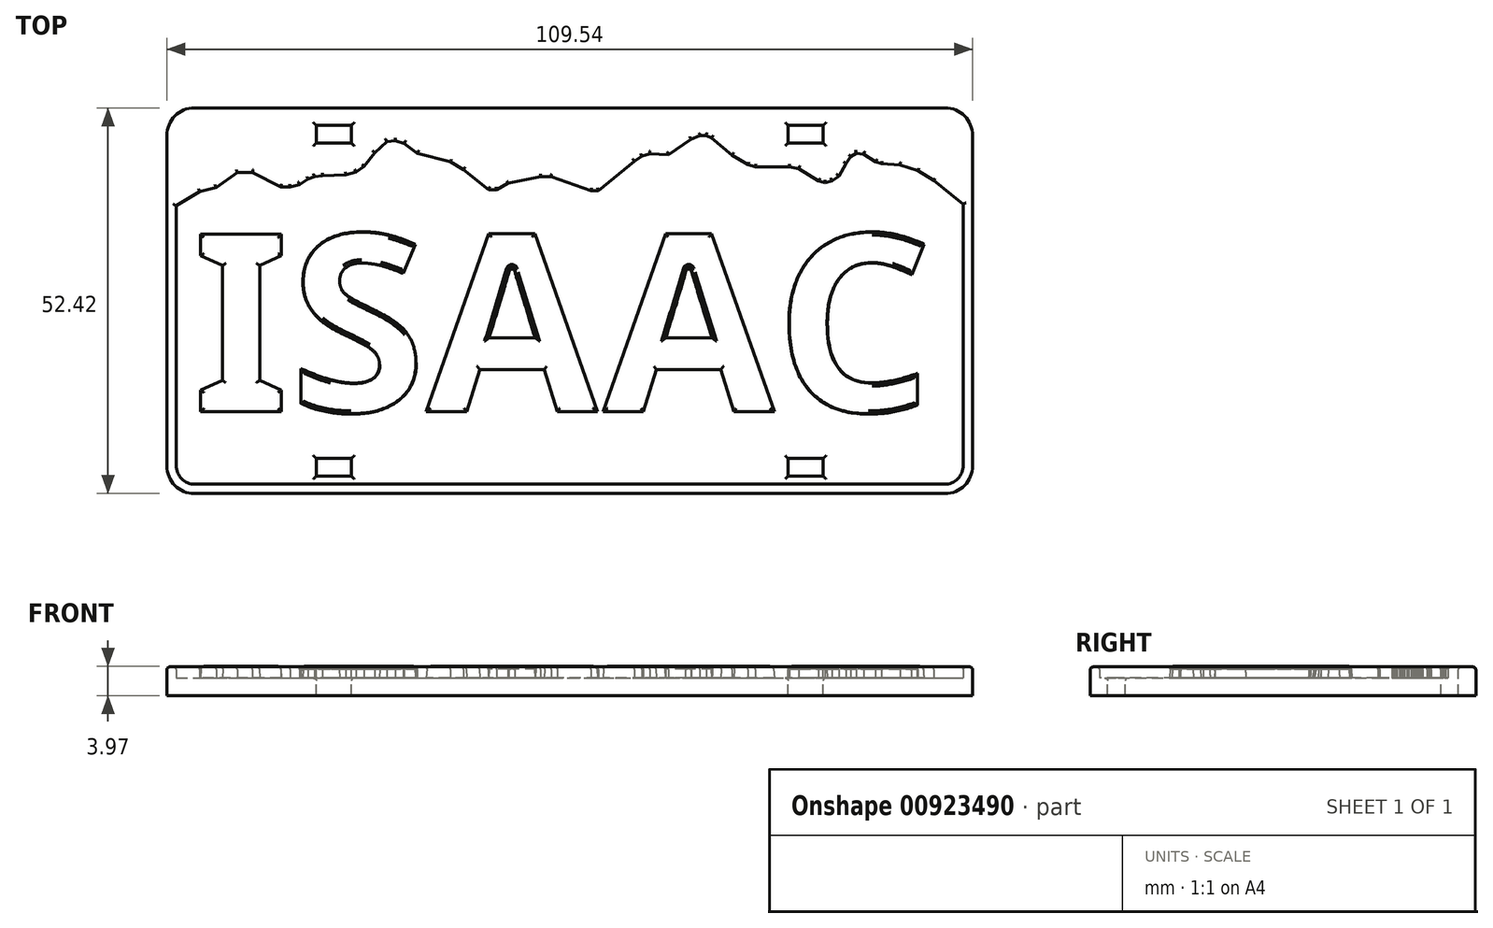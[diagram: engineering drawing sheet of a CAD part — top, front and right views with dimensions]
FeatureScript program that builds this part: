
annotation { "Feature Type Name" : "Feature", "Feature Type Description" : "" }
export const myFeature = defineFeature(function(context is Context, id is Id, definition is map)
    precondition{}
    {
        {
            var Q0;
            Q0=qCreatedBy(makeId("Top.planeOp"),FACE);
            var sketch = newSketch(context, id + "F0", { "sketchPlane" : qUnion([Q0])});
            skLineSegment(sketch, "E0", {"start": v(54.77, -22.46) * mm, "end": v(54.77, 22.46) * mm});
            skArc(sketch, "E1", {"start": v(54.77, 22.46) * mm, "mid": v(53.68, 25.11) * mm, "end": v(51.02, 26.21) * mm});
            skLineSegment(sketch, "E2", {"start": v(51.02, 26.21) * mm, "end": v(-51.02, 26.21) * mm});
            skArc(sketch, "E3", {"start": v(-51.02, 26.21) * mm, "mid": v(-53.68, 25.11) * mm, "end": v(-54.77, 22.46) * mm});
            skLineSegment(sketch, "E4", {"start": v(-54.77, 22.46) * mm, "end": v(-54.77, -22.46) * mm});
            skArc(sketch, "E5", {"start": v(-54.77, -22.46) * mm, "mid": v(-53.54, -25.24) * mm, "end": v(-50.64, -26.2) * mm});
            skLineSegment(sketch, "E6", {"start": v(-50.64, -26.2) * mm, "end": v(51.04, -26.2) * mm});
            skArc(sketch, "E7", {"start": v(51.02, -26.21) * mm, "mid": v(53.68, -25.11) * mm, "end": v(54.77, -22.46) * mm});
            skLineSegment(sketch, "E8", {"start": v(-54.77, 12.13) * mm, "end": v(-50.31, 14.84) * mm});
            skLineSegment(sketch, "E9", {"start": v(-50.31, 14.84) * mm, "end": v(-48.06, 15.4) * mm});
            skLineSegment(sketch, "E10", {"start": v(-48.06, 15.4) * mm, "end": v(-45.2, 17.44) * mm});
            skLineSegment(sketch, "E11", {"start": v(-45.2, 17.44) * mm, "end": v(-43.14, 17.44) * mm});
            skLineSegment(sketch, "E12", {"start": v(-43.14, 17.44) * mm, "end": v(-39.3, 15.5) * mm});
            skLineSegment(sketch, "E13", {"start": v(-39.3, 15.5) * mm, "end": v(-38.03, 15.49) * mm});
            skLineSegment(sketch, "E14", {"start": v(-38.03, 15.49) * mm, "end": v(-36.75, 15.8) * mm});
            skLineSegment(sketch, "E15", {"start": v(-36.75, 15.8) * mm, "end": v(-35.57, 16.54) * mm});
            skLineSegment(sketch, "E16", {"start": v(-35.57, 16.54) * mm, "end": v(-34.73, 16.88) * mm});
            skLineSegment(sketch, "E17", {"start": v(-34.73, 16.88) * mm, "end": v(-33.6, 17.01) * mm});
            skLineSegment(sketch, "E18", {"start": v(-33.6, 17.01) * mm, "end": v(-30.43, 17.11) * mm});
            skLineSegment(sketch, "E19", {"start": v(-29.05, 17.5) * mm, "end": v(-27.98, 18.27) * mm});
            skLineSegment(sketch, "E20", {"start": v(-27.98, 18.27) * mm, "end": v(-26.53, 20.14) * mm});
            skLineSegment(sketch, "E21", {"start": v(-26.53, 20.14) * mm, "end": v(-24.88, 21.63) * mm});
            skLineSegment(sketch, "E22", {"start": v(-24.88, 21.63) * mm, "end": v(-23.73, 21.77) * mm});
            skLineSegment(sketch, "E23", {"start": v(-22.5, 21.4) * mm, "end": v(-20.72, 20.04) * mm});
            skLineSegment(sketch, "E24", {"start": v(-16.23, 18.87) * mm, "end": v(-14.45, 17.85) * mm});
            skLineSegment(sketch, "E25", {"start": v(-14.45, 17.85) * mm, "end": v(-11.02, 15.1) * mm});
            skLineSegment(sketch, "E26", {"start": v(-11.02, 15.1) * mm, "end": v(-9.93, 15.1) * mm});
            skLineSegment(sketch, "E27", {"start": v(-9.93, 15.1) * mm, "end": v(-8.4, 15.96) * mm});
            skLineSegment(sketch, "E28", {"start": v(-8.4, 15.96) * mm, "end": v(-3.94, 16.85) * mm});
            skLineSegment(sketch, "E29", {"start": v(-3.94, 16.85) * mm, "end": v(-2.54, 16.85) * mm});
            skLineSegment(sketch, "E30", {"start": v(-2.54, 16.85) * mm, "end": v(2.9, 14.97) * mm});
            skLineSegment(sketch, "E31", {"start": v(2.9, 14.97) * mm, "end": v(3.92, 14.97) * mm});
            skLineSegment(sketch, "E32", {"start": v(3.92, 14.97) * mm, "end": v(8.8, 18.97) * mm});
            skLineSegment(sketch, "E33", {"start": v(8.8, 18.97) * mm, "end": v(9.82, 19.64) * mm});
            skLineSegment(sketch, "E34", {"start": v(9.82, 19.64) * mm, "end": v(10.9, 19.97) * mm});
            skLineSegment(sketch, "E35", {"start": v(10.9, 19.97) * mm, "end": v(13.43, 19.86) * mm});
            skLineSegment(sketch, "E36", {"start": v(16.5, 21.96) * mm, "end": v(17.71, 22.42) * mm});
            skLineSegment(sketch, "E37", {"start": v(17.71, 22.42) * mm, "end": v(18.56, 22.45) * mm});
            skLineSegment(sketch, "E38", {"start": v(18.56, 22.45) * mm, "end": v(19.28, 22.13) * mm});
            skLineSegment(sketch, "E39", {"start": v(19.28, 22.13) * mm, "end": v(22.05, 19.8) * mm});
            skLineSegment(sketch, "E40", {"start": v(22.05, 19.8) * mm, "end": v(24.2, 18.5) * mm});
            skLineSegment(sketch, "E41", {"start": v(24.2, 18.5) * mm, "end": v(25.23, 18.2) * mm});
            skLineSegment(sketch, "E42", {"start": v(25.23, 18.2) * mm, "end": v(29.85, 18.2) * mm});
            skLineSegment(sketch, "E43", {"start": v(29.85, 18.2) * mm, "end": v(31.13, 17.95) * mm});
            skLineSegment(sketch, "E44", {"start": v(31.13, 17.95) * mm, "end": v(33.84, 16.27) * mm});
            skLineSegment(sketch, "E45", {"start": v(33.84, 16.27) * mm, "end": v(34.73, 16.06) * mm});
            skLineSegment(sketch, "E46", {"start": v(34.73, 16.06) * mm, "end": v(35.67, 16.3) * mm});
            skLineSegment(sketch, "E47", {"start": v(35.67, 16.3) * mm, "end": v(36.58, 16.95) * mm});
            skLineSegment(sketch, "E48", {"start": v(36.58, 16.95) * mm, "end": v(37.58, 18.67) * mm});
            skLineSegment(sketch, "E49", {"start": v(38.22, 19.58) * mm, "end": v(38.96, 20.06) * mm});
            skLineSegment(sketch, "E50", {"start": v(38.96, 20.06) * mm, "end": v(39.94, 19.92) * mm});
            skLineSegment(sketch, "E51", {"start": v(41.58, 18.88) * mm, "end": v(42.4, 18.61) * mm});
            skLineSegment(sketch, "E52", {"start": v(42.4, 18.61) * mm, "end": v(44.9, 18.47) * mm});
            skLineSegment(sketch, "E53", {"start": v(44.9, 18.47) * mm, "end": v(47.31, 17.68) * mm});
            skLineSegment(sketch, "E54", {"start": v(47.31, 17.68) * mm, "end": v(49.47, 16.33) * mm});
            skLineSegment(sketch, "E55", {"start": v(49.47, 16.33) * mm, "end": v(51.88, 14.42) * mm});
            skLineSegment(sketch, "E56", {"start": v(51.88, 14.42) * mm, "end": v(53.78, 12.92) * mm});
            skLineSegment(sketch, "E57", {"start": v(53.78, 12.92) * mm, "end": v(54.77, 12.06) * mm});
            skLineSegment(sketch, "E58", {"start": v(-20.72, 20.04) * mm, "end": v(-16.23, 18.87) * mm});
            skLineSegment(sketch, "E59", {"start": v(16.5, 21.96) * mm, "end": v(13.43, 19.86) * mm});
            skLineSegment(sketch, "E60", {"start": v(-22.5, 21.4) * mm, "end": v(-23.73, 21.77) * mm});
            skLineSegment(sketch, "E61", {"start": v(-29.05, 17.5) * mm, "end": v(-30.43, 17.11) * mm});
            skLineSegment(sketch, "E62", {"start": v(37.58, 18.67) * mm, "end": v(38.22, 19.58) * mm});
            skLineSegment(sketch, "E63", {"start": v(41.58, 18.88) * mm, "end": v(39.94, 19.92) * mm});
            skSolve(sketch);
        }
        {
            var Q0;
            Q0=qCreatedBy(makeId("Top.planeOp"),FACE);
            var sketch = newSketch(context, id + "F1", { "sketchPlane" : qUnion([Q0])});
            skLineSegment(sketch, "E64", {"start": v(54.77, -22.46) * mm, "end": v(54.77, 22.46) * mm});
            skArc(sketch, "E65", {"start": v(54.77, 22.46) * mm, "mid": v(53.68, 25.11) * mm, "end": v(51.02, 26.21) * mm});
            skLineSegment(sketch, "E66", {"start": v(51.02, 26.21) * mm, "end": v(-51.02, 26.21) * mm});
            skArc(sketch, "E67", {"start": v(-51.02, 26.21) * mm, "mid": v(-53.68, 25.11) * mm, "end": v(-54.77, 22.46) * mm});
            skLineSegment(sketch, "E68", {"start": v(-54.77, 22.46) * mm, "end": v(-54.77, -22.46) * mm});
            skArc(sketch, "E69", {"start": v(-54.77, -22.46) * mm, "mid": v(-53.68, -25.11) * mm, "end": v(-51.02, -26.21) * mm});
            skLineSegment(sketch, "E70", {"start": v(-51.02, -26.21) * mm, "end": v(51.02, -26.21) * mm});
            skArc(sketch, "E71", {"start": v(51.02, -26.21) * mm, "mid": v(53.68, -25.11) * mm, "end": v(54.77, -22.46) * mm});
            skLineSegment(sketch, "E72.0", {"start": v(50.96, 24.94) * mm, "end": v(-50.96, 24.94) * mm, "construction": true});
            skLineSegment(sketch, "E72.1", {"start": v(53.5, -22.4) * mm, "end": v(53.5, 22.4) * mm, "construction": true});
            skLineSegment(sketch, "E72.2", {"start": v(-50.96, -24.94) * mm, "end": v(50.96, -24.94) * mm, "construction": true});
            skLineSegment(sketch, "E72.3", {"start": v(-53.5, 22.4) * mm, "end": v(-53.5, -22.4) * mm, "construction": true});
            skPoint(sketch, "E73.visualSharp", {"position": v(-53.5, 24.94) * mm});
            skArc(sketch, "E73.filletArc", {"start": v(-50.96, 24.94) * mm, "mid": v(-52.76, 24.2) * mm, "end": v(-53.5, 22.4) * mm, "construction": true});
            skPoint(sketch, "E74.visualSharp", {"position": v(-53.5, -24.94) * mm});
            skArc(sketch, "E74.filletArc", {"start": v(-53.5, -22.4) * mm, "mid": v(-52.76, -24.2) * mm, "end": v(-50.96, -24.94) * mm, "construction": true});
            skPoint(sketch, "E75.visualSharp", {"position": v(53.5, -24.94) * mm});
            skArc(sketch, "E75.filletArc", {"start": v(50.96, -24.94) * mm, "mid": v(52.76, -24.2) * mm, "end": v(53.5, -22.4) * mm, "construction": true});
            skPoint(sketch, "E76.visualSharp", {"position": v(53.5, 24.94) * mm});
            skArc(sketch, "E76.filletArc", {"start": v(53.5, 22.4) * mm, "mid": v(52.76, 24.2) * mm, "end": v(50.96, 24.94) * mm, "construction": true});
            skSolve(sketch);
        }
        {
            var Q0;
            {var subQ3=sQuery(id+"F0.wireOp",EDGE,"E1");Q0=makeQuery(id+"F0.imprint","IMPRINT",FACE,{"disambiguationData":[TD([[makeQuery(id+"F0.imprint","IMPRINT",EDGE,{"derivedFrom":subQ3}),1.0]])]});}
            extrude(context, id + "F2", {"entities" : qUnion([Q0]), "depth" : 1.52 * mm, "offsetDistance" : 25.4 * mm});
        }
        {
            var Q0;
            Q0=qSketchRegion(id+"F1",true);
            extrude(context, id + "F3", {"entities" : qUnion([Q0]), "operationType" : NewBodyOperationType.ADD, "oppositeDirection" : true, "depth" : 2.38 * mm, "offsetDistance" : 25.4 * mm});
        }
        {
            var Q0;
            {var subQ58=sQuery(id+"F0.wireOp",EDGE,"E0");var subQ59=sQuery(id+"F1.wireOp",EDGE,"E64");var subQ60=sQuery(id+"F1.wireOp",EDGE,"E65");var subQ61=sQuery(id+"F1.wireOp",EDGE,"E68");var subQ62=sQuery(id+"F1.wireOp",EDGE,"E69");var subQ63=sQuery(id+"F1.wireOp",EDGE,"E70");var subQ64=sQuery(id+"F1.wireOp",EDGE,"E71");Q0=makeQuery(id+"F3.boolean.opBoolean","SPLIT",FACE,{"disambiguationData":[TD([makeQuery(id+"F2.opExtrude","SWEPT_FACE",FACE,{"disambiguationData":[OSD([subQ58])]})])],"derivedFrom":makeQuery(id+"F3.opExtrude","CAP_FACE",FACE,{"disambiguationData":[OSD([subQ59,subQ60,sQuery(id+"F1.wireOp",EDGE,"E66"),sQuery(id+"F1.wireOp",EDGE,"E67"),subQ61,subQ62,subQ63,subQ64])],"isStart":true})});}
            var sketch = newSketch(context, id + "F4", { "sketchPlane" : qUnion([Q0])});
            skLineSegment(sketch, "E77", {"start": v(54.77, -22.46) * mm, "end": v(54.77, 12.06) * mm});
            skLineSegment(sketch, "E78", {"start": v(-54.77, 12.13) * mm, "end": v(-54.77, -22.46) * mm});
            skArc(sketch, "E79", {"start": v(-54.77, -22.46) * mm, "mid": v(-53.68, -25.11) * mm, "end": v(-51.02, -26.21) * mm});
            skLineSegment(sketch, "E80", {"start": v(-51.02, -26.21) * mm, "end": v(51.02, -26.21) * mm});
            skArc(sketch, "E81", {"start": v(51.02, -26.21) * mm, "mid": v(53.68, -25.11) * mm, "end": v(54.77, -22.46) * mm});
            skLineSegment(sketch, "E82.1", {"start": v(53.5, -22.4) * mm, "end": v(53.5, 13.14) * mm});
            skLineSegment(sketch, "E82.2", {"start": v(-50.96, -24.94) * mm, "end": v(50.96, -24.94) * mm});
            skLineSegment(sketch, "E82.3", {"start": v(-53.5, 12.9) * mm, "end": v(-53.5, -22.4) * mm});
            skPoint(sketch, "E83.visualSharp", {"position": v(-53.5, 24.94) * mm});
            skPoint(sketch, "E84.visualSharp", {"position": v(-53.5, -24.94) * mm});
            skArc(sketch, "E84.filletArc", {"start": v(-53.5, -22.4) * mm, "mid": v(-52.76, -24.2) * mm, "end": v(-50.96, -24.94) * mm});
            skPoint(sketch, "E85.visualSharp", {"position": v(53.5, -24.94) * mm});
            skArc(sketch, "E85.filletArc", {"start": v(50.96, -24.94) * mm, "mid": v(52.76, -24.2) * mm, "end": v(53.5, -22.4) * mm});
            skPoint(sketch, "E86.visualSharp", {"position": v(53.5, 24.94) * mm});
            skLineSegment(sketch, "E87", {"start": v(-54.77, 12.13) * mm, "end": v(-53.5, 12.9) * mm});
            skLineSegment(sketch, "E88", {"start": v(53.5, 13.14) * mm, "end": v(53.78, 12.92) * mm});
            skLineSegment(sketch, "E89", {"start": v(53.78, 12.92) * mm, "end": v(54.77, 12.06) * mm});
            skSolve(sketch);
        }
        {
            var Q0;
            Q0=qSketchRegion(id+"F4",true);
            extrude(context, id + "F5", {"entities" : qUnion([Q0]), "operationType" : NewBodyOperationType.ADD, "depth" : 1.52 * mm, "offsetDistance" : 25.4 * mm});
        }
        {
            var Q0;
            Q0=makeQuery(id+"F5.boolean.opBoolean","MERGE",FACE,{"derivedFrom":[makeQuery(id+"F2.opExtrude","CAP_FACE",FACE,{"disambiguationData":[OSD([sQuery(id+"F0.wireOp",EDGE,"E0"),sQuery(id+"F0.wireOp",EDGE,"E1"),sQuery(id+"F0.wireOp",EDGE,"E2"),sQuery(id+"F0.wireOp",EDGE,"E3"),sQuery(id+"F0.wireOp",EDGE,"E4"),sQuery(id+"F0.wireOp",EDGE,"E8"),sQuery(id+"F0.wireOp",EDGE,"E9"),sQuery(id+"F0.wireOp",EDGE,"E10"),sQuery(id+"F0.wireOp",EDGE,"E11"),sQuery(id+"F0.wireOp",EDGE,"E12"),sQuery(id+"F0.wireOp",EDGE,"E13"),sQuery(id+"F0.wireOp",EDGE,"E14"),sQuery(id+"F0.wireOp",EDGE,"E15"),sQuery(id+"F0.wireOp",EDGE,"E16"),sQuery(id+"F0.wireOp",EDGE,"E17"),sQuery(id+"F0.wireOp",EDGE,"E18"),sQuery(id+"F0.wireOp",EDGE,"7b9f405e-0691-426e-9c9e-a5372cf0836a"),sQuery(id+"F0.wireOp",EDGE,"E19"),sQuery(id+"F0.wireOp",EDGE,"E20"),sQuery(id+"F0.wireOp",EDGE,"E21"),sQuery(id+"F0.wireOp",EDGE,"E22"),sQuery(id+"F0.wireOp",EDGE,"b3dec5b1-662c-4d50-a13c-af7b7760114a"),sQuery(id+"F0.wireOp",EDGE,"E23"),sQuery(id+"F0.wireOp",EDGE,"4d9ee76e-0833-4cdc-b1a8-2d4ce76e6521"),sQuery(id+"F0.wireOp",EDGE,"E24"),sQuery(id+"F0.wireOp",EDGE,"E25"),sQuery(id+"F0.wireOp",EDGE,"E26"),sQuery(id+"F0.wireOp",EDGE,"E27"),sQuery(id+"F0.wireOp",EDGE,"E28"),sQuery(id+"F0.wireOp",EDGE,"E29"),sQuery(id+"F0.wireOp",EDGE,"E30"),sQuery(id+"F0.wireOp",EDGE,"E31"),sQuery(id+"F0.wireOp",EDGE,"E32"),sQuery(id+"F0.wireOp",EDGE,"E33"),sQuery(id+"F0.wireOp",EDGE,"E34"),sQuery(id+"F0.wireOp",EDGE,"E35"),sQuery(id+"F0.wireOp",EDGE,"55551997-bb9e-4b94-90c5-def3cb147476"),sQuery(id+"F0.wireOp",EDGE,"E36"),sQuery(id+"F0.wireOp",EDGE,"E37"),sQuery(id+"F0.wireOp",EDGE,"E38"),sQuery(id+"F0.wireOp",EDGE,"E39"),sQuery(id+"F0.wireOp",EDGE,"E40"),sQuery(id+"F0.wireOp",EDGE,"E41"),sQuery(id+"F0.wireOp",EDGE,"E42"),sQuery(id+"F0.wireOp",EDGE,"E43"),sQuery(id+"F0.wireOp",EDGE,"E44"),sQuery(id+"F0.wireOp",EDGE,"E45"),sQuery(id+"F0.wireOp",EDGE,"E46"),sQuery(id+"F0.wireOp",EDGE,"E47"),sQuery(id+"F0.wireOp",EDGE,"E48"),sQuery(id+"F0.wireOp",EDGE,"513b7cbe-d979-4e22-b277-f3c42ccdbda1"),sQuery(id+"F0.wireOp",EDGE,"E49"),sQuery(id+"F0.wireOp",EDGE,"E50"),sQuery(id+"F0.wireOp",EDGE,"0d842e13-672c-40e3-aae4-28923e78d4e0"),sQuery(id+"F0.wireOp",EDGE,"E51"),sQuery(id+"F0.wireOp",EDGE,"E52"),sQuery(id+"F0.wireOp",EDGE,"E53"),sQuery(id+"F0.wireOp",EDGE,"E54"),sQuery(id+"F0.wireOp",EDGE,"E55"),sQuery(id+"F0.wireOp",EDGE,"E56"),sQuery(id+"F0.wireOp",EDGE,"E57")])],"isStart":false}),makeQuery(id+"F5.opExtrude","CAP_FACE",FACE,{"disambiguationData":[OSD([sQuery(id+"F4.wireOp",EDGE,"E77"),sQuery(id+"F4.wireOp",EDGE,"E78"),sQuery(id+"F4.wireOp",EDGE,"E79"),sQuery(id+"F4.wireOp",EDGE,"E80"),sQuery(id+"F4.wireOp",EDGE,"E81"),sQuery(id+"F4.wireOp",EDGE,"E82.1"),sQuery(id+"F4.wireOp",EDGE,"E82.2"),sQuery(id+"F4.wireOp",EDGE,"E82.3"),sQuery(id+"F4.wireOp",EDGE,"E84.filletArc"),sQuery(id+"F4.wireOp",EDGE,"E85.filletArc"),sQuery(id+"F4.wireOp",EDGE,"E87"),sQuery(id+"F4.wireOp",EDGE,"E88"),sQuery(id+"F4.wireOp",EDGE,"E89")])],"isStart":false})]});
            var sketch = newSketch(context, id + "F6", { "sketchPlane" : qUnion([Q0])});
            skLineSegment(sketch, "E90.bottom", {"start": v(-34.45, 23.83) * mm, "end": v(-29.7, 23.83) * mm});
            skLineSegment(sketch, "E90.top", {"start": v(-34.45, 21.45) * mm, "end": v(-29.7, 21.45) * mm});
            skLineSegment(sketch, "E90.left", {"start": v(-34.45, 23.83) * mm, "end": v(-34.45, 21.45) * mm});
            skLineSegment(sketch, "E90.right", {"start": v(-29.7, 23.83) * mm, "end": v(-29.7, 21.45) * mm});
            skLineSegment(sketch, "E91", {"start": v(0, 26.21) * mm, "end": v(0, -26.21) * mm, "construction": true});
            skLineSegment(sketch, "E92.MirrorCS", {"start": v(34.45, 23.83) * mm, "end": v(34.45, 21.45) * mm});
            skLineSegment(sketch, "E93.MirrorCS", {"start": v(29.7, 23.83) * mm, "end": v(29.7, 21.45) * mm});
            skLineSegment(sketch, "E94.MirrorCS", {"start": v(34.45, 21.45) * mm, "end": v(29.7, 21.45) * mm});
            skLineSegment(sketch, "E95.MirrorCS", {"start": v(34.45, 23.83) * mm, "end": v(29.7, 23.83) * mm});
            skLineSegment(sketch, "E96", {"start": v(0, 0) * mm, "end": v(-59.23, 0) * mm, "construction": true});
            skLineSegment(sketch, "E97", {"start": v(0, 0) * mm, "end": v(56.47, 0) * mm, "construction": true});
            skLineSegment(sketch, "E98.MirrorCS", {"start": v(-34.45, -23.83) * mm, "end": v(-29.7, -23.83) * mm});
            skLineSegment(sketch, "E99.MirrorCS", {"start": v(-34.45, -23.83) * mm, "end": v(-34.45, -21.45) * mm});
            skLineSegment(sketch, "E100.MirrorCS", {"start": v(-34.45, -21.45) * mm, "end": v(-29.7, -21.45) * mm});
            skLineSegment(sketch, "E101.MirrorCS", {"start": v(-29.7, -23.83) * mm, "end": v(-29.7, -21.45) * mm});
            skLineSegment(sketch, "E102.MirrorCS", {"start": v(29.7, -23.83) * mm, "end": v(29.7, -21.45) * mm});
            skLineSegment(sketch, "E103.MirrorCS", {"start": v(34.45, -23.83) * mm, "end": v(29.7, -23.83) * mm});
            skLineSegment(sketch, "E104.MirrorCS", {"start": v(34.45, -23.83) * mm, "end": v(34.45, -21.45) * mm});
            skLineSegment(sketch, "E105.MirrorCS", {"start": v(34.45, -21.45) * mm, "end": v(29.7, -21.45) * mm});
            skSolve(sketch);
        }
        {
            var Q0;
            Q0=qSketchRegion(id+"F6",true);
            extrude(context, id + "F7", {"entities" : qUnion([Q0]), "operationType" : NewBodyOperationType.REMOVE, "endBound" : BoundingType.THROUGH_ALL, "oppositeDirection" : true, "depth" : 25.4 * mm, "offsetDistance" : 25.4 * mm});
        }
        {
            var Q0;
            Q0=makeQuery(id+"F3.opExtrude","CAP_FACE",FACE,{"disambiguationData":[OSD([sQuery(id+"F1.wireOp",EDGE,"E64"),sQuery(id+"F1.wireOp",EDGE,"E65"),sQuery(id+"F1.wireOp",EDGE,"E66"),sQuery(id+"F1.wireOp",EDGE,"E67"),sQuery(id+"F1.wireOp",EDGE,"E68"),sQuery(id+"F1.wireOp",EDGE,"E69"),sQuery(id+"F1.wireOp",EDGE,"E70"),sQuery(id+"F1.wireOp",EDGE,"E71")])],"isStart":true});
            var sketch = newSketch(context, id + "F8", { "sketchPlane" : qUnion([Q0])});
            skText(sketch, "E106", { "text": "ISAAC", "fontName": "NotoSans-Bold.ttf"});
            const initialGuessF8  = {"E106": [-0.05126, -0.01508, 1, 0, 0.02432]};
            skSetInitialGuess(sketch, initialGuessF8);
            skSolve(sketch);
        }
        {
            var Q0;
            Q0=qSketchRegion(id+"F8",true);
            extrude(context, id + "F9", {"entities" : qUnion([Q0]), "operationType" : NewBodyOperationType.ADD, "depth" : 1.59 * mm, "offsetDistance" : 25.4 * mm, "hasDraft" : true, "draftAngle" : 3 * degree, "draftPullDirection" : true});
        }
        {
            var Q0;
            Q0=makeQuery(id+"F5.boolean.opBoolean","MERGE",FACE,{"derivedFrom":[makeQuery(id+"F2.opExtrude","CAP_FACE",FACE,{"disambiguationData":[OSD([sQuery(id+"F0.wireOp",EDGE,"E0"),sQuery(id+"F0.wireOp",EDGE,"E1"),sQuery(id+"F0.wireOp",EDGE,"E2"),sQuery(id+"F0.wireOp",EDGE,"E3"),sQuery(id+"F0.wireOp",EDGE,"E4"),sQuery(id+"F0.wireOp",EDGE,"E8"),sQuery(id+"F0.wireOp",EDGE,"E9"),sQuery(id+"F0.wireOp",EDGE,"E10"),sQuery(id+"F0.wireOp",EDGE,"E11"),sQuery(id+"F0.wireOp",EDGE,"E12"),sQuery(id+"F0.wireOp",EDGE,"E13"),sQuery(id+"F0.wireOp",EDGE,"E14"),sQuery(id+"F0.wireOp",EDGE,"E15"),sQuery(id+"F0.wireOp",EDGE,"E16"),sQuery(id+"F0.wireOp",EDGE,"E17"),sQuery(id+"F0.wireOp",EDGE,"E18"),sQuery(id+"F0.wireOp",EDGE,"7b9f405e-0691-426e-9c9e-a5372cf0836a"),sQuery(id+"F0.wireOp",EDGE,"E19"),sQuery(id+"F0.wireOp",EDGE,"E20"),sQuery(id+"F0.wireOp",EDGE,"E21"),sQuery(id+"F0.wireOp",EDGE,"E22"),sQuery(id+"F0.wireOp",EDGE,"b3dec5b1-662c-4d50-a13c-af7b7760114a"),sQuery(id+"F0.wireOp",EDGE,"E23"),sQuery(id+"F0.wireOp",EDGE,"4d9ee76e-0833-4cdc-b1a8-2d4ce76e6521"),sQuery(id+"F0.wireOp",EDGE,"E24"),sQuery(id+"F0.wireOp",EDGE,"E25"),sQuery(id+"F0.wireOp",EDGE,"E26"),sQuery(id+"F0.wireOp",EDGE,"E27"),sQuery(id+"F0.wireOp",EDGE,"E28"),sQuery(id+"F0.wireOp",EDGE,"E29"),sQuery(id+"F0.wireOp",EDGE,"E30"),sQuery(id+"F0.wireOp",EDGE,"E31"),sQuery(id+"F0.wireOp",EDGE,"E32"),sQuery(id+"F0.wireOp",EDGE,"E33"),sQuery(id+"F0.wireOp",EDGE,"E34"),sQuery(id+"F0.wireOp",EDGE,"E35"),sQuery(id+"F0.wireOp",EDGE,"55551997-bb9e-4b94-90c5-def3cb147476"),sQuery(id+"F0.wireOp",EDGE,"E36"),sQuery(id+"F0.wireOp",EDGE,"E37"),sQuery(id+"F0.wireOp",EDGE,"E38"),sQuery(id+"F0.wireOp",EDGE,"E39"),sQuery(id+"F0.wireOp",EDGE,"E40"),sQuery(id+"F0.wireOp",EDGE,"E41"),sQuery(id+"F0.wireOp",EDGE,"E42"),sQuery(id+"F0.wireOp",EDGE,"E43"),sQuery(id+"F0.wireOp",EDGE,"E44"),sQuery(id+"F0.wireOp",EDGE,"E45"),sQuery(id+"F0.wireOp",EDGE,"E46"),sQuery(id+"F0.wireOp",EDGE,"E47"),sQuery(id+"F0.wireOp",EDGE,"E48"),sQuery(id+"F0.wireOp",EDGE,"513b7cbe-d979-4e22-b277-f3c42ccdbda1"),sQuery(id+"F0.wireOp",EDGE,"E49"),sQuery(id+"F0.wireOp",EDGE,"E50"),sQuery(id+"F0.wireOp",EDGE,"0d842e13-672c-40e3-aae4-28923e78d4e0"),sQuery(id+"F0.wireOp",EDGE,"E51"),sQuery(id+"F0.wireOp",EDGE,"E52"),sQuery(id+"F0.wireOp",EDGE,"E53"),sQuery(id+"F0.wireOp",EDGE,"E54"),sQuery(id+"F0.wireOp",EDGE,"E55"),sQuery(id+"F0.wireOp",EDGE,"E56"),sQuery(id+"F0.wireOp",EDGE,"E57")])],"isStart":false}),makeQuery(id+"F5.opExtrude","CAP_FACE",FACE,{"disambiguationData":[OSD([sQuery(id+"F4.wireOp",EDGE,"E77"),sQuery(id+"F4.wireOp",EDGE,"E78"),sQuery(id+"F4.wireOp",EDGE,"E79"),sQuery(id+"F4.wireOp",EDGE,"E80"),sQuery(id+"F4.wireOp",EDGE,"E81"),sQuery(id+"F4.wireOp",EDGE,"E82.1"),sQuery(id+"F4.wireOp",EDGE,"E82.2"),sQuery(id+"F4.wireOp",EDGE,"E82.3"),sQuery(id+"F4.wireOp",EDGE,"E84.filletArc"),sQuery(id+"F4.wireOp",EDGE,"E85.filletArc"),sQuery(id+"F4.wireOp",EDGE,"E87"),sQuery(id+"F4.wireOp",EDGE,"E88"),sQuery(id+"F4.wireOp",EDGE,"E89")])],"isStart":false})]});
            var Q1;
            {var subQ0=sQuery(id+"F1.wireOp",EDGE,"E64");var subQ1=sQuery(id+"F1.wireOp",EDGE,"E68");var subQ2=sQuery(id+"F1.wireOp",EDGE,"E69");var subQ3=sQuery(id+"F1.wireOp",EDGE,"E70");var subQ4=sQuery(id+"F1.wireOp",EDGE,"E71");Q1=makeQuery(id+"F7.boolean.opBoolean","INTERSECT",EDGE,{"derivedFrom":[makeQuery(id+"F3.boolean.opBoolean","SPLIT",FACE,{"disambiguationData":[TD([makeQuery(id+"F2.opExtrude","SWEPT_FACE",FACE,{"disambiguationData":[OSD([sQuery(id+"F0.wireOp",EDGE,"E0")])]})])],"derivedFrom":makeQuery(id+"F3.opExtrude","CAP_FACE",FACE,{"disambiguationData":[OSD([subQ0,sQuery(id+"F1.wireOp",EDGE,"E65"),sQuery(id+"F1.wireOp",EDGE,"E66"),sQuery(id+"F1.wireOp",EDGE,"E67"),subQ1,subQ2,subQ3,subQ4])],"isStart":true})}),makeQuery(id+"F7.opExtrude","SWEPT_FACE",FACE,{"disambiguationData":[OSD([sQuery(id+"F6.wireOp",EDGE,"E100.MirrorCS")])]})]});}
            var Q2;
            {var subQ0=sQuery(id+"F1.wireOp",EDGE,"E64");var subQ1=sQuery(id+"F1.wireOp",EDGE,"E68");var subQ2=sQuery(id+"F1.wireOp",EDGE,"E69");var subQ3=sQuery(id+"F1.wireOp",EDGE,"E70");var subQ4=sQuery(id+"F1.wireOp",EDGE,"E71");Q2=makeQuery(id+"F7.boolean.opBoolean","INTERSECT",EDGE,{"derivedFrom":[makeQuery(id+"F3.boolean.opBoolean","SPLIT",FACE,{"disambiguationData":[TD([makeQuery(id+"F2.opExtrude","SWEPT_FACE",FACE,{"disambiguationData":[OSD([sQuery(id+"F0.wireOp",EDGE,"E0")])]})])],"derivedFrom":makeQuery(id+"F3.opExtrude","CAP_FACE",FACE,{"disambiguationData":[OSD([subQ0,sQuery(id+"F1.wireOp",EDGE,"E65"),sQuery(id+"F1.wireOp",EDGE,"E66"),sQuery(id+"F1.wireOp",EDGE,"E67"),subQ1,subQ2,subQ3,subQ4])],"isStart":true})}),makeQuery(id+"F7.opExtrude","SWEPT_FACE",FACE,{"disambiguationData":[OSD([sQuery(id+"F6.wireOp",EDGE,"E99.MirrorCS")])]})]});}
            var Q3;
            {var subQ0=sQuery(id+"F1.wireOp",EDGE,"E64");var subQ1=sQuery(id+"F1.wireOp",EDGE,"E68");var subQ2=sQuery(id+"F1.wireOp",EDGE,"E69");var subQ3=sQuery(id+"F1.wireOp",EDGE,"E70");var subQ4=sQuery(id+"F1.wireOp",EDGE,"E71");Q3=makeQuery(id+"F7.boolean.opBoolean","INTERSECT",EDGE,{"derivedFrom":[makeQuery(id+"F3.boolean.opBoolean","SPLIT",FACE,{"disambiguationData":[TD([makeQuery(id+"F2.opExtrude","SWEPT_FACE",FACE,{"disambiguationData":[OSD([sQuery(id+"F0.wireOp",EDGE,"E0")])]})])],"derivedFrom":makeQuery(id+"F3.opExtrude","CAP_FACE",FACE,{"disambiguationData":[OSD([subQ0,sQuery(id+"F1.wireOp",EDGE,"E65"),sQuery(id+"F1.wireOp",EDGE,"E66"),sQuery(id+"F1.wireOp",EDGE,"E67"),subQ1,subQ2,subQ3,subQ4])],"isStart":true})}),makeQuery(id+"F7.opExtrude","SWEPT_FACE",FACE,{"disambiguationData":[OSD([sQuery(id+"F6.wireOp",EDGE,"E98.MirrorCS")])]})]});}
            var Q4;
            {var subQ0=sQuery(id+"F1.wireOp",EDGE,"E64");var subQ1=sQuery(id+"F1.wireOp",EDGE,"E68");var subQ2=sQuery(id+"F1.wireOp",EDGE,"E69");var subQ3=sQuery(id+"F1.wireOp",EDGE,"E70");var subQ4=sQuery(id+"F1.wireOp",EDGE,"E71");Q4=makeQuery(id+"F7.boolean.opBoolean","INTERSECT",EDGE,{"derivedFrom":[makeQuery(id+"F3.boolean.opBoolean","SPLIT",FACE,{"disambiguationData":[TD([makeQuery(id+"F2.opExtrude","SWEPT_FACE",FACE,{"disambiguationData":[OSD([sQuery(id+"F0.wireOp",EDGE,"E0")])]})])],"derivedFrom":makeQuery(id+"F3.opExtrude","CAP_FACE",FACE,{"disambiguationData":[OSD([subQ0,sQuery(id+"F1.wireOp",EDGE,"E65"),sQuery(id+"F1.wireOp",EDGE,"E66"),sQuery(id+"F1.wireOp",EDGE,"E67"),subQ1,subQ2,subQ3,subQ4])],"isStart":true})}),makeQuery(id+"F7.opExtrude","SWEPT_FACE",FACE,{"disambiguationData":[OSD([sQuery(id+"F6.wireOp",EDGE,"E101.MirrorCS")])]})]});}
            var Q5;
            {var subQ0=sQuery(id+"F1.wireOp",EDGE,"E64");var subQ1=sQuery(id+"F1.wireOp",EDGE,"E68");var subQ2=sQuery(id+"F1.wireOp",EDGE,"E69");var subQ3=sQuery(id+"F1.wireOp",EDGE,"E70");var subQ4=sQuery(id+"F1.wireOp",EDGE,"E71");Q5=makeQuery(id+"F7.boolean.opBoolean","INTERSECT",EDGE,{"derivedFrom":[makeQuery(id+"F3.boolean.opBoolean","SPLIT",FACE,{"disambiguationData":[TD([makeQuery(id+"F2.opExtrude","SWEPT_FACE",FACE,{"disambiguationData":[OSD([sQuery(id+"F0.wireOp",EDGE,"E0")])]})])],"derivedFrom":makeQuery(id+"F3.opExtrude","CAP_FACE",FACE,{"disambiguationData":[OSD([subQ0,sQuery(id+"F1.wireOp",EDGE,"E65"),sQuery(id+"F1.wireOp",EDGE,"E66"),sQuery(id+"F1.wireOp",EDGE,"E67"),subQ1,subQ2,subQ3,subQ4])],"isStart":true})}),makeQuery(id+"F7.opExtrude","SWEPT_FACE",FACE,{"disambiguationData":[OSD([sQuery(id+"F6.wireOp",EDGE,"E102.MirrorCS")])]})]});}
            var Q6;
            {var subQ0=sQuery(id+"F1.wireOp",EDGE,"E64");var subQ1=sQuery(id+"F1.wireOp",EDGE,"E68");var subQ2=sQuery(id+"F1.wireOp",EDGE,"E69");var subQ3=sQuery(id+"F1.wireOp",EDGE,"E70");var subQ4=sQuery(id+"F1.wireOp",EDGE,"E71");Q6=makeQuery(id+"F7.boolean.opBoolean","INTERSECT",EDGE,{"derivedFrom":[makeQuery(id+"F3.boolean.opBoolean","SPLIT",FACE,{"disambiguationData":[TD([makeQuery(id+"F2.opExtrude","SWEPT_FACE",FACE,{"disambiguationData":[OSD([sQuery(id+"F0.wireOp",EDGE,"E0")])]})])],"derivedFrom":makeQuery(id+"F3.opExtrude","CAP_FACE",FACE,{"disambiguationData":[OSD([subQ0,sQuery(id+"F1.wireOp",EDGE,"E65"),sQuery(id+"F1.wireOp",EDGE,"E66"),sQuery(id+"F1.wireOp",EDGE,"E67"),subQ1,subQ2,subQ3,subQ4])],"isStart":true})}),makeQuery(id+"F7.opExtrude","SWEPT_FACE",FACE,{"disambiguationData":[OSD([sQuery(id+"F6.wireOp",EDGE,"E105.MirrorCS")])]})]});}
            var Q7;
            {var subQ0=sQuery(id+"F1.wireOp",EDGE,"E64");var subQ1=sQuery(id+"F1.wireOp",EDGE,"E68");var subQ2=sQuery(id+"F1.wireOp",EDGE,"E69");var subQ3=sQuery(id+"F1.wireOp",EDGE,"E70");var subQ4=sQuery(id+"F1.wireOp",EDGE,"E71");Q7=makeQuery(id+"F7.boolean.opBoolean","INTERSECT",EDGE,{"derivedFrom":[makeQuery(id+"F3.boolean.opBoolean","SPLIT",FACE,{"disambiguationData":[TD([makeQuery(id+"F2.opExtrude","SWEPT_FACE",FACE,{"disambiguationData":[OSD([sQuery(id+"F0.wireOp",EDGE,"E0")])]})])],"derivedFrom":makeQuery(id+"F3.opExtrude","CAP_FACE",FACE,{"disambiguationData":[OSD([subQ0,sQuery(id+"F1.wireOp",EDGE,"E65"),sQuery(id+"F1.wireOp",EDGE,"E66"),sQuery(id+"F1.wireOp",EDGE,"E67"),subQ1,subQ2,subQ3,subQ4])],"isStart":true})}),makeQuery(id+"F7.opExtrude","SWEPT_FACE",FACE,{"disambiguationData":[OSD([sQuery(id+"F6.wireOp",EDGE,"E104.MirrorCS")])]})]});}
            var Q8;
            {var subQ0=sQuery(id+"F1.wireOp",EDGE,"E64");var subQ1=sQuery(id+"F1.wireOp",EDGE,"E68");var subQ2=sQuery(id+"F1.wireOp",EDGE,"E69");var subQ3=sQuery(id+"F1.wireOp",EDGE,"E70");var subQ4=sQuery(id+"F1.wireOp",EDGE,"E71");Q8=makeQuery(id+"F7.boolean.opBoolean","INTERSECT",EDGE,{"derivedFrom":[makeQuery(id+"F3.boolean.opBoolean","SPLIT",FACE,{"disambiguationData":[TD([makeQuery(id+"F2.opExtrude","SWEPT_FACE",FACE,{"disambiguationData":[OSD([sQuery(id+"F0.wireOp",EDGE,"E0")])]})])],"derivedFrom":makeQuery(id+"F3.opExtrude","CAP_FACE",FACE,{"disambiguationData":[OSD([subQ0,sQuery(id+"F1.wireOp",EDGE,"E65"),sQuery(id+"F1.wireOp",EDGE,"E66"),sQuery(id+"F1.wireOp",EDGE,"E67"),subQ1,subQ2,subQ3,subQ4])],"isStart":true})}),makeQuery(id+"F7.opExtrude","SWEPT_FACE",FACE,{"disambiguationData":[OSD([sQuery(id+"F6.wireOp",EDGE,"E103.MirrorCS")])]})]});}
            var Q9;
            Q9=makeQuery(id+"F9.opExtrude","CAP_FACE",FACE,{"disambiguationData":[OSD([sQuery(id+"F8.wireOp",EDGE,"E106.sketch_text.stroke-0"),sQuery(id+"F8.wireOp",EDGE,"E106.sketch_text.stroke-1"),sQuery(id+"F8.wireOp",EDGE,"E106.sketch_text.stroke-2"),sQuery(id+"F8.wireOp",EDGE,"E106.sketch_text.stroke-3"),sQuery(id+"F8.wireOp",EDGE,"E106.sketch_text.stroke-4"),sQuery(id+"F8.wireOp",EDGE,"E106.sketch_text.stroke-5"),sQuery(id+"F8.wireOp",EDGE,"E106.sketch_text.stroke-6"),sQuery(id+"F8.wireOp",EDGE,"E106.sketch_text.stroke-7"),sQuery(id+"F8.wireOp",EDGE,"E106.sketch_text.stroke-8"),sQuery(id+"F8.wireOp",EDGE,"E106.sketch_text.stroke-9"),sQuery(id+"F8.wireOp",EDGE,"E106.sketch_text.stroke-10"),sQuery(id+"F8.wireOp",EDGE,"E106.sketch_text.stroke-11"),sQuery(id+"F8.wireOp",EDGE,"E106.sketch_text.stroke-12"),sQuery(id+"F8.wireOp",EDGE,"E106.sketch_text.stroke-13"),sQuery(id+"F8.wireOp",EDGE,"E106.sketch_text.stroke-14")])],"isStart":false});
            var Q10;
            Q10=makeQuery(id+"F9.opExtrude","CAP_FACE",FACE,{"disambiguationData":[OSD([sQuery(id+"F8.wireOp",EDGE,"E106.sketch_text.stroke-15"),sQuery(id+"F8.wireOp",EDGE,"E106.sketch_text.stroke-16"),sQuery(id+"F8.wireOp",EDGE,"E106.sketch_text.stroke-17"),sQuery(id+"F8.wireOp",EDGE,"E106.sketch_text.stroke-18"),sQuery(id+"F8.wireOp",EDGE,"E106.sketch_text.stroke-19"),sQuery(id+"F8.wireOp",EDGE,"E106.sketch_text.stroke-20"),sQuery(id+"F8.wireOp",EDGE,"E106.sketch_text.stroke-21"),sQuery(id+"F8.wireOp",EDGE,"E106.sketch_text.stroke-22"),sQuery(id+"F8.wireOp",EDGE,"E106.sketch_text.stroke-23"),sQuery(id+"F8.wireOp",EDGE,"E106.sketch_text.stroke-24"),sQuery(id+"F8.wireOp",EDGE,"E106.sketch_text.stroke-25"),sQuery(id+"F8.wireOp",EDGE,"E106.sketch_text.stroke-26"),sQuery(id+"F8.wireOp",EDGE,"E106.sketch_text.stroke-27"),sQuery(id+"F8.wireOp",EDGE,"E106.sketch_text.stroke-28")])],"isStart":false});
            var Q11;
            Q11=makeQuery(id+"F9.opExtrude","CAP_FACE",FACE,{"disambiguationData":[OSD([sQuery(id+"F8.wireOp",EDGE,"E106.sketch_text.stroke-29"),sQuery(id+"F8.wireOp",EDGE,"E106.sketch_text.stroke-30"),sQuery(id+"F8.wireOp",EDGE,"E106.sketch_text.stroke-31"),sQuery(id+"F8.wireOp",EDGE,"E106.sketch_text.stroke-32"),sQuery(id+"F8.wireOp",EDGE,"E106.sketch_text.stroke-33"),sQuery(id+"F8.wireOp",EDGE,"E106.sketch_text.stroke-34"),sQuery(id+"F8.wireOp",EDGE,"E106.sketch_text.stroke-35"),sQuery(id+"F8.wireOp",EDGE,"E106.sketch_text.stroke-36"),sQuery(id+"F8.wireOp",EDGE,"E106.sketch_text.stroke-37"),sQuery(id+"F8.wireOp",EDGE,"E106.sketch_text.stroke-38"),sQuery(id+"F8.wireOp",EDGE,"E106.sketch_text.stroke-39"),sQuery(id+"F8.wireOp",EDGE,"E106.sketch_text.stroke-40"),sQuery(id+"F8.wireOp",EDGE,"E106.sketch_text.stroke-41"),sQuery(id+"F8.wireOp",EDGE,"E106.sketch_text.stroke-42")])],"isStart":false});
            var Q12;
            Q12=makeQuery(id+"F9.opExtrude","CAP_FACE",FACE,{"disambiguationData":[OSD([sQuery(id+"F8.wireOp",EDGE,"E106.sketch_text.stroke-57"),sQuery(id+"F8.wireOp",EDGE,"E106.sketch_text.stroke-58"),sQuery(id+"F8.wireOp",EDGE,"E106.sketch_text.stroke-59"),sQuery(id+"F8.wireOp",EDGE,"E106.sketch_text.stroke-60"),sQuery(id+"F8.wireOp",EDGE,"E106.sketch_text.stroke-61"),sQuery(id+"F8.wireOp",EDGE,"E106.sketch_text.stroke-62"),sQuery(id+"F8.wireOp",EDGE,"E106.sketch_text.stroke-63"),sQuery(id+"F8.wireOp",EDGE,"E106.sketch_text.stroke-64"),sQuery(id+"F8.wireOp",EDGE,"E106.sketch_text.stroke-65"),sQuery(id+"F8.wireOp",EDGE,"E106.sketch_text.stroke-66"),sQuery(id+"F8.wireOp",EDGE,"E106.sketch_text.stroke-67"),sQuery(id+"F8.wireOp",EDGE,"E106.sketch_text.stroke-68"),sQuery(id+"F8.wireOp",EDGE,"E106.sketch_text.stroke-69"),sQuery(id+"F8.wireOp",EDGE,"E106.sketch_text.stroke-70")])],"isStart":false});
            var Q13;
            Q13=makeQuery(id+"F9.opExtrude","CAP_FACE",FACE,{"disambiguationData":[OSD([sQuery(id+"F8.wireOp",EDGE,"E106.sketch_text.stroke-71"),sQuery(id+"F8.wireOp",EDGE,"E106.sketch_text.stroke-72"),sQuery(id+"F8.wireOp",EDGE,"E106.sketch_text.stroke-73"),sQuery(id+"F8.wireOp",EDGE,"E106.sketch_text.stroke-74"),sQuery(id+"F8.wireOp",EDGE,"E106.sketch_text.stroke-75"),sQuery(id+"F8.wireOp",EDGE,"E106.sketch_text.stroke-76"),sQuery(id+"F8.wireOp",EDGE,"E106.sketch_text.stroke-77"),sQuery(id+"F8.wireOp",EDGE,"E106.sketch_text.stroke-78"),sQuery(id+"F8.wireOp",EDGE,"E106.sketch_text.stroke-79"),sQuery(id+"F8.wireOp",EDGE,"E106.sketch_text.stroke-80"),sQuery(id+"F8.wireOp",EDGE,"E106.sketch_text.stroke-81"),sQuery(id+"F8.wireOp",EDGE,"E106.sketch_text.stroke-82"),sQuery(id+"F8.wireOp",EDGE,"E106.sketch_text.stroke-83"),sQuery(id+"F8.wireOp",EDGE,"E106.sketch_text.stroke-84"),sQuery(id+"F8.wireOp",EDGE,"E106.sketch_text.stroke-85"),sQuery(id+"F8.wireOp",EDGE,"E106.sketch_text.stroke-86"),sQuery(id+"F8.wireOp",EDGE,"E106.sketch_text.stroke-87"),sQuery(id+"F8.wireOp",EDGE,"E106.sketch_text.stroke-88"),sQuery(id+"F8.wireOp",EDGE,"E106.sketch_text.stroke-89")])],"isStart":false});
            var Q14;
            Q14=makeQuery(id+"F9.opExtrude","CAP_FACE",FACE,{"disambiguationData":[OSD([sQuery(id+"F8.wireOp",EDGE,"E106.sketch_text.stroke-43"),sQuery(id+"F8.wireOp",EDGE,"E106.sketch_text.stroke-44"),sQuery(id+"F8.wireOp",EDGE,"E106.sketch_text.stroke-45"),sQuery(id+"F8.wireOp",EDGE,"E106.sketch_text.stroke-46"),sQuery(id+"F8.wireOp",EDGE,"E106.sketch_text.stroke-47"),sQuery(id+"F8.wireOp",EDGE,"E106.sketch_text.stroke-48"),sQuery(id+"F8.wireOp",EDGE,"E106.sketch_text.stroke-49"),sQuery(id+"F8.wireOp",EDGE,"E106.sketch_text.stroke-50"),sQuery(id+"F8.wireOp",EDGE,"E106.sketch_text.stroke-51"),sQuery(id+"F8.wireOp",EDGE,"E106.sketch_text.stroke-52"),sQuery(id+"F8.wireOp",EDGE,"E106.sketch_text.stroke-53"),sQuery(id+"F8.wireOp",EDGE,"E106.sketch_text.stroke-54"),sQuery(id+"F8.wireOp",EDGE,"E106.sketch_text.stroke-55"),sQuery(id+"F8.wireOp",EDGE,"E106.sketch_text.stroke-56")])],"isStart":false});
            var Q15;
            Q15=makeQuery(id+"F9.opExtrude","CAP_FACE",FACE,{"disambiguationData":[OSD([sQuery(id+"F8.wireOp",EDGE,"E106.sketch_text.stroke-12"),sQuery(id+"F8.wireOp",EDGE,"E106.sketch_text.stroke-13"),sQuery(id+"F8.wireOp",EDGE,"E106.sketch_text.stroke-14"),sQuery(id+"F8.wireOp",EDGE,"E106.sketch_text.stroke-15"),sQuery(id+"F8.wireOp",EDGE,"E106.sketch_text.stroke-16"),sQuery(id+"F8.wireOp",EDGE,"E106.sketch_text.stroke-17")])],"isStart":false});
            var Q16;
            Q16=makeQuery(id+"F9.opExtrude","SWEPT_EDGE",EDGE,{"disambiguationData":[OSD([sQuery(id+"F8.wireOp",EDGE,"E106.sketch_text.stroke-49"),sQuery(id+"F8.wireOp",EDGE,"E106.sketch_text.stroke-50")])]});
            var Q17;
            Q17=makeQuery(id+"F9.opExtrude","SWEPT_EDGE",EDGE,{"disambiguationData":[OSD([sQuery(id+"F8.wireOp",EDGE,"E106.sketch_text.stroke-61"),sQuery(id+"F8.wireOp",EDGE,"E106.sketch_text.stroke-62")])]});
            fillet(context, id + "F10", {"entities" : qUnion([Q0, Q1, Q2, Q3, Q4, Q5, Q6, Q7, Q8, Q9, Q10, Q11, Q12, Q13, Q14, Q15, Q16, Q17]), "radius" : 0.38 * mm, "tangentPropagation" : true, "allowEdgeOverflow" : false});
        }
    });
